# Revit family: Table-Teknion-Zones_ZNTFS-R2015
name_source: partatom
category: Furniture
revit_build: Autodesk Revit Architecture 2015 (Build: 20140323_1530(x64)
units: mm (PartAtom-declared; Revit-internal decimal feet)

## types (3) — shared parameters
Assembly Code = E2020200
Height = 36"
Manufacturer = Teknion
Manufacturer Fax = 416.661.4586
Part Number = ZNTFS
Product Documentation Link = http://www.teknion.com
Product Line = Zones
Product Page URL = http://www.teknion.com
Series = Zones
Sustainability Data = http://www.teknion.com
URL = http://www.teknion.com
Warranty = http://www.teknion.com

## per-type parameters (varying)
| type | Depth | Description | Model | Width |
| 27" Depth | 27" | Soft Square Coffee Table, 27" Depth | ZNTFS27 | 27" |
| 36" Depth | 36" | Soft Square Coffee Table, 36" Depth | ZNTFS36 | 36" |
| 24" Depth | 24" | Soft Square Coffee Table, 24" Depth | ZNTFS24 | 24" |

## geometry (parser evidence)
native form markers: Blend x14, Sweep x2
no freeform markers — native parametric forms only
